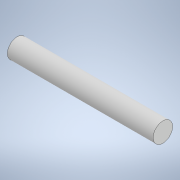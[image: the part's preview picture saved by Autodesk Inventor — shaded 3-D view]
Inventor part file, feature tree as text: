
AUTODESK INVENTOR PART (.ipt)
format: ipt  version: 2021 (Build 250183000, 183)  size: 89,600 bytes
history: native  units: mm
features: extrude x1, sketch x1
ambient origin geometry x8: Origin, YZ Plane, XZ Plane, XY Plane, X Axis, Y Axis, Z Axis, Center Point
bodies: Solid1 (feature_tree)
feature tree (2):
  extrude  "Extrusion1"  Depth=60.0mm TaperAngle=0.0deg
  sketch  "Sketch1"  dims[d0=8.0mm d1=60.0mm d2=0.0mm]
